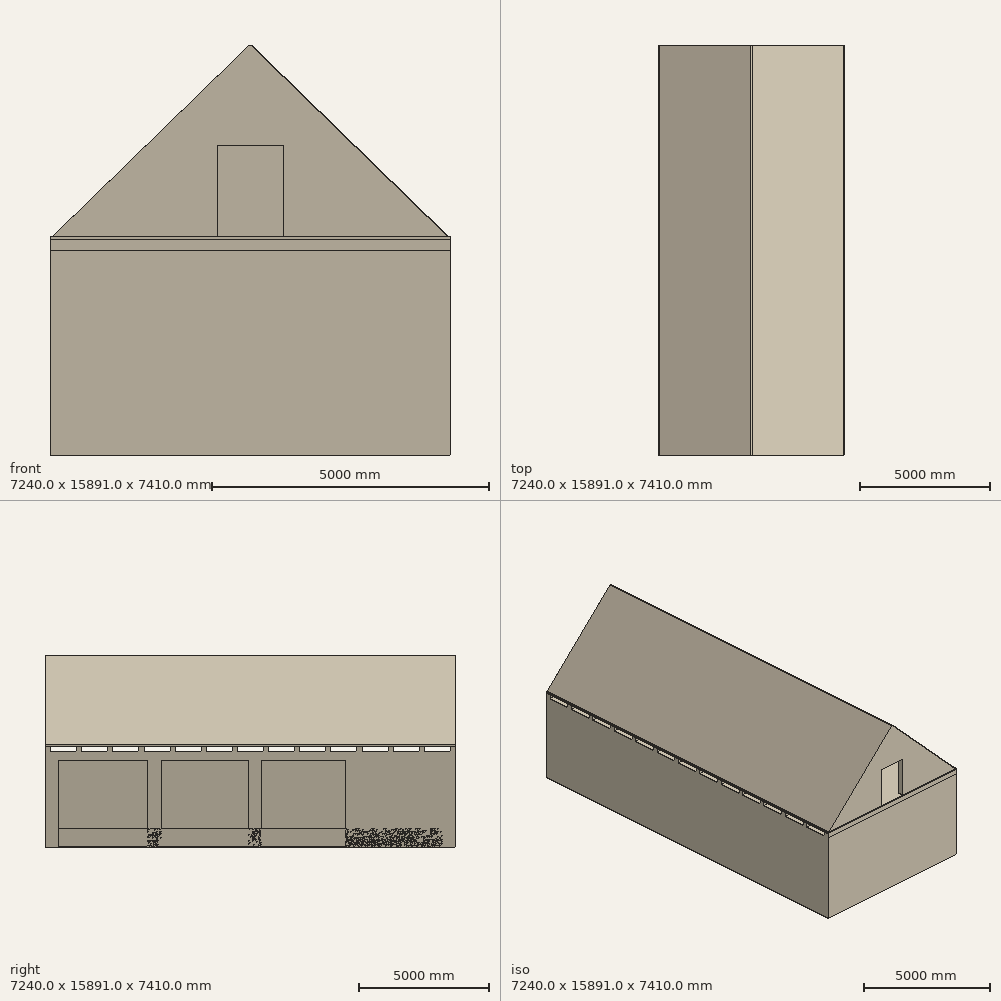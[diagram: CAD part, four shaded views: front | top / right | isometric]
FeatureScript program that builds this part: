
annotation { "Feature Type Name" : "Feature", "Feature Type Description" : "" }
export const myFeature = defineFeature(function(context is Context, id is Id, definition is map)
    precondition{}
    {
        {
            var Q0;
            Q0=qCreatedBy(makeId("Top.planeOp"),FACE);
            var sketch = newSketch(context, id + "F0", { "sketchPlane" : qUnion([Q0])});
            skLineSegment(sketch, "E0.bottom", {"start": v(-3374.35, 6436.17) * mm, "end": v(2825.65, 6436.17) * mm});
            skLineSegment(sketch, "E0.top", {"start": v(-3374.35, -8413.83) * mm, "end": v(2825.65, -8413.83) * mm});
            skLineSegment(sketch, "E0.left", {"start": v(-3374.35, 6436.17) * mm, "end": v(-3374.35, -8413.83) * mm});
            skLineSegment(sketch, "E0.right", {"start": v(2825.65, 6436.17) * mm, "end": v(2825.65, -8413.83) * mm});
            skLineSegment(sketch, "E1.0", {"start": v(-3894.35, 6956.17) * mm, "end": v(-3894.35, -8933.83) * mm});
            skLineSegment(sketch, "E1.1", {"start": v(-3894.35, 6956.17) * mm, "end": v(3345.65, 6956.17) * mm});
            skLineSegment(sketch, "E1.2", {"start": v(3345.65, 6956.17) * mm, "end": v(3345.65, -8933.83) * mm});
            skLineSegment(sketch, "E1.3", {"start": v(-3894.35, -8933.83) * mm, "end": v(3345.65, -8933.83) * mm});
            skLineSegment(sketch, "E2", {"start": v(2825.65, -8413.83) * mm, "end": v(3345.65, -8413.83) * mm});
            skLineSegment(sketch, "E3", {"start": v(2825.65, -4963.83) * mm, "end": v(3345.65, -4963.83) * mm});
            skLineSegment(sketch, "E4", {"start": v(2825.65, -4443.83) * mm, "end": v(3345.65, -4443.83) * mm});
            skLineSegment(sketch, "E5", {"start": v(2825.65, -1063.83) * mm, "end": v(3345.65, -1063.83) * mm});
            skLineSegment(sketch, "E6", {"start": v(2825.65, -543.83) * mm, "end": v(3345.65, -543.83) * mm});
            skLineSegment(sketch, "E7", {"start": v(2825.65, 2696.17) * mm, "end": v(3345.65, 2696.17) * mm});
            skSolve(sketch);
        }
        {
            var Q0;
            {var subQ5=sQuery(id+"F0.wireOp",EDGE,"E0.bottom");Q0=makeQuery(id+"F0.imprint","IMPRINT",FACE,{"disambiguationData":[TD([[makeQuery(id+"F0.imprint","IMPRINT",EDGE,{"derivedFrom":subQ5}),1.0]])]});}
            var Q1;
            {var subQ1=sQuery(id+"F0.wireOp",EDGE,"E0.bottom");Q1=makeQuery(id+"F0.imprint","IMPRINT",FACE,{"disambiguationData":[TD([[makeQuery(id+"F0.imprint","IMPRINT",EDGE,{"derivedFrom":subQ1}),-1.0]])]});}
            var Q2;
            {var subQ0=sQuery(id+"F0.wireOp",EDGE,"E6");Q2=makeQuery(id+"F0.imprint","IMPRINT",FACE,{"disambiguationData":[TD([[makeQuery(id+"F0.imprint","IMPRINT",EDGE,{"derivedFrom":subQ0}),1.0]])]});}
            var Q3;
            {var subQ0=sQuery(id+"F0.wireOp",EDGE,"E5");Q3=makeQuery(id+"F0.imprint","IMPRINT",FACE,{"disambiguationData":[TD([[makeQuery(id+"F0.imprint","IMPRINT",EDGE,{"derivedFrom":subQ0}),1.0]])]});}
            var Q4;
            {var subQ0=sQuery(id+"F0.wireOp",EDGE,"E4");Q4=makeQuery(id+"F0.imprint","IMPRINT",FACE,{"disambiguationData":[TD([[makeQuery(id+"F0.imprint","IMPRINT",EDGE,{"derivedFrom":subQ0}),1.0]])]});}
            var Q5;
            {var subQ0=sQuery(id+"F0.wireOp",EDGE,"E2");Q5=makeQuery(id+"F0.imprint","IMPRINT",FACE,{"disambiguationData":[TD([[makeQuery(id+"F0.imprint","IMPRINT",EDGE,{"derivedFrom":subQ0}),1.0]])]});}
            var Q6;
            {var subQ0=sQuery(id+"F0.wireOp",EDGE,"E3");Q6=makeQuery(id+"F0.imprint","IMPRINT",FACE,{"disambiguationData":[TD([[makeQuery(id+"F0.imprint","IMPRINT",EDGE,{"derivedFrom":subQ0}),1.0]])]});}
            extrude(context, id + "F1", {"entities" : qUnion([Q0, Q1, Q2, Q3, Q4, Q5, Q6]), "oppositeDirection" : true, "depth" : 10 * mm, "offsetDistance" : 25 * mm});
        }
        {
            var Q0;
            {var subQ0=sQuery(id+"F0.wireOp",EDGE,"E5");Q0=makeQuery(id+"F0.imprint","IMPRINT",FACE,{"disambiguationData":[TD([[makeQuery(id+"F0.imprint","IMPRINT",EDGE,{"derivedFrom":subQ0}),1.0]])]});}
            var Q1;
            {var subQ0=sQuery(id+"F0.wireOp",EDGE,"E3");Q1=makeQuery(id+"F0.imprint","IMPRINT",FACE,{"disambiguationData":[TD([[makeQuery(id+"F0.imprint","IMPRINT",EDGE,{"derivedFrom":subQ0}),1.0]])]});}
            var Q2;
            {var subQ5=sQuery(id+"F0.wireOp",EDGE,"E0.bottom");Q2=makeQuery(id+"F0.imprint","IMPRINT",FACE,{"disambiguationData":[TD([[makeQuery(id+"F0.imprint","IMPRINT",EDGE,{"derivedFrom":subQ5}),1.0]])]});}
            extrude(context, id + "F2", {"entities" : qUnion([Q0, Q1, Q2]), "operationType" : NewBodyOperationType.ADD, "depth" : 3350 * mm, "offsetDistance" : 25 * mm});
        }
        {
            var Q0;
            Q0=makeQuery(id+"F2.opExtrude","CAP_FACE",FACE,{"disambiguationData":[OSD([sQuery(id+"F0.wireOp",EDGE,"E0.bottom"),sQuery(id+"F0.wireOp",EDGE,"E0.top"),sQuery(id+"F0.wireOp",EDGE,"E0.left"),sQuery(id+"F0.wireOp",EDGE,"E0.right"),sQuery(id+"F0.wireOp",EDGE,"E1.0"),sQuery(id+"F0.wireOp",EDGE,"E1.1"),sQuery(id+"F0.wireOp",EDGE,"E1.2"),sQuery(id+"F0.wireOp",EDGE,"E1.3"),sQuery(id+"F0.wireOp",EDGE,"E2"),sQuery(id+"F0.wireOp",EDGE,"E7")])],"isStart":false});
            var sketch = newSketch(context, id + "F3", { "sketchPlane" : qUnion([Q0])});
            skLineSegment(sketch, "E8.bottom", {"start": v(-3894.35, 6956.17) * mm, "end": v(3345.65, 6956.17) * mm});
            skLineSegment(sketch, "E8.top", {"start": v(-3894.35, -8933.83) * mm, "end": v(3345.65, -8933.83) * mm});
            skLineSegment(sketch, "E8.left", {"start": v(-3894.35, 6956.17) * mm, "end": v(-3894.35, -8933.83) * mm});
            skLineSegment(sketch, "E8.right", {"start": v(3345.65, 6956.17) * mm, "end": v(3345.65, -8933.83) * mm});
            skLineSegment(sketch, "E9.bottom", {"start": v(2825.65, 6436.17) * mm, "end": v(-3374.35, 6436.17) * mm});
            skLineSegment(sketch, "E9.top", {"start": v(2825.65, -8413.83) * mm, "end": v(-3374.35, -8413.83) * mm});
            skLineSegment(sketch, "E9.left", {"start": v(2825.65, 6436.17) * mm, "end": v(2825.65, -8413.83) * mm});
            skLineSegment(sketch, "E9.right", {"start": v(-3374.35, 6436.17) * mm, "end": v(-3374.35, -8413.83) * mm});
            skSolve(sketch);
        }
        {
            var Q0;
            {var subQ8=sQuery(id+"F3.wireOp",EDGE,"E8.bottom");Q0=makeQuery(id+"F3.imprint","IMPRINT",FACE,{"disambiguationData":[TD([[makeQuery(id+"F3.imprint","IMPRINT",EDGE,{"derivedFrom":subQ8}),-1.0]])]});}
            var Q1;
            {var subQ3=makeQuery(id+"F2.opExtrude","CAP_EDGE",EDGE,{"disambiguationData":[OSD([sQuery(id+"F0.wireOp",EDGE,"E7")])],"isStart":false});Q1=makeQuery(id+"F3.imprint","IMPRINT",FACE,{"disambiguationData":[TD([[makeQuery(id+"F3.imprint","IMPRINT",EDGE,{"derivedFrom":subQ3}),-1.0]])]});}
            extrude(context, id + "F4", {"entities" : qUnion([Q0, Q1]), "operationType" : NewBodyOperationType.ADD, "depth" : 350 * mm, "offsetDistance" : 25 * mm});
        }
        {
            var Q0;
            Q0=makeQuery(id+"F4.opExtrude","CAP_FACE",FACE,{"disambiguationData":[OSD([sQuery(id+"F3.wireOp",EDGE,"E8.bottom"),sQuery(id+"F3.wireOp",EDGE,"E8.top"),sQuery(id+"F3.wireOp",EDGE,"E8.left"),sQuery(id+"F3.wireOp",EDGE,"E8.right"),sQuery(id+"F3.wireOp",EDGE,"E9.bottom"),sQuery(id+"F3.wireOp",EDGE,"E9.top"),sQuery(id+"F3.wireOp",EDGE,"E9.left"),sQuery(id+"F3.wireOp",EDGE,"E9.right")])],"isStart":false});
            var sketch = newSketch(context, id + "F5", { "sketchPlane" : qUnion([Q0])});
            skLineSegment(sketch, "E10.bottom", {"start": v(3345.65, 6956.17) * mm, "end": v(-3894.35, 6956.17) * mm});
            skLineSegment(sketch, "E10.top", {"start": v(3345.65, 6756.17) * mm, "end": v(-3894.35, 6756.17) * mm});
            skLineSegment(sketch, "E10.left", {"start": v(3345.65, 6956.17) * mm, "end": v(3345.65, 6756.17) * mm});
            skLineSegment(sketch, "E10.right", {"start": v(-3894.35, 6956.17) * mm, "end": v(-3894.35, 6756.17) * mm});
            skLineSegment(sketch, "E11.bottom", {"start": v(3345.65, 5749.17) * mm, "end": v(-3894.35, 5749.17) * mm});
            skLineSegment(sketch, "E11.top", {"start": v(3345.65, 5549.17) * mm, "end": v(-3894.35, 5549.17) * mm});
            skLineSegment(sketch, "E11.left", {"start": v(3345.65, 5749.17) * mm, "end": v(3345.65, 5549.17) * mm});
            skLineSegment(sketch, "E11.right", {"start": v(-3894.35, 5749.17) * mm, "end": v(-3894.35, 5549.17) * mm});
            skLineSegment(sketch, "E12.bottom", {"start": v(3345.65, 4542.17) * mm, "end": v(-3894.35, 4542.17) * mm});
            skLineSegment(sketch, "E12.top", {"start": v(3345.65, 4342.17) * mm, "end": v(-3894.35, 4342.17) * mm});
            skLineSegment(sketch, "E12.left", {"start": v(3345.65, 4542.17) * mm, "end": v(3345.65, 4342.17) * mm});
            skLineSegment(sketch, "E12.right", {"start": v(-3894.35, 4542.17) * mm, "end": v(-3894.35, 4342.17) * mm});
            skLineSegment(sketch, "E13.bottom", {"start": v(3345.65, 3335.17) * mm, "end": v(-3894.35, 3335.17) * mm});
            skLineSegment(sketch, "E13.top", {"start": v(3345.65, 3135.17) * mm, "end": v(-3894.35, 3135.17) * mm});
            skLineSegment(sketch, "E13.left", {"start": v(3345.65, 3335.17) * mm, "end": v(3345.65, 3135.17) * mm});
            skLineSegment(sketch, "E13.right", {"start": v(-3894.35, 3335.17) * mm, "end": v(-3894.35, 3135.17) * mm});
            skLineSegment(sketch, "E14.bottom", {"start": v(3345.65, 2128.17) * mm, "end": v(-3894.35, 2128.17) * mm});
            skLineSegment(sketch, "E14.top", {"start": v(3345.65, 1928.17) * mm, "end": v(-3894.35, 1928.17) * mm});
            skLineSegment(sketch, "E14.left", {"start": v(3345.65, 2128.17) * mm, "end": v(3345.65, 1928.17) * mm});
            skLineSegment(sketch, "E14.right", {"start": v(-3894.35, 2128.17) * mm, "end": v(-3894.35, 1928.17) * mm});
            skLineSegment(sketch, "E15.bottom", {"start": v(3345.65, 921.17) * mm, "end": v(-3894.35, 921.17) * mm});
            skLineSegment(sketch, "E15.top", {"start": v(3345.65, 721.17) * mm, "end": v(-3894.35, 721.17) * mm});
            skLineSegment(sketch, "E15.left", {"start": v(3345.65, 921.17) * mm, "end": v(3345.65, 721.17) * mm});
            skLineSegment(sketch, "E15.right", {"start": v(-3894.35, 921.17) * mm, "end": v(-3894.35, 721.17) * mm});
            skLineSegment(sketch, "E16.bottom", {"start": v(3345.65, -285.83) * mm, "end": v(-3894.35, -285.83) * mm});
            skLineSegment(sketch, "E16.top", {"start": v(3345.65, -485.83) * mm, "end": v(-3894.35, -485.83) * mm});
            skLineSegment(sketch, "E16.left", {"start": v(3345.65, -285.83) * mm, "end": v(3345.65, -485.83) * mm});
            skLineSegment(sketch, "E16.right", {"start": v(-3894.35, -285.83) * mm, "end": v(-3894.35, -485.83) * mm});
            skLineSegment(sketch, "E17.bottom", {"start": v(3345.65, -1492.83) * mm, "end": v(-3894.35, -1492.83) * mm});
            skLineSegment(sketch, "E17.top", {"start": v(3345.65, -1692.83) * mm, "end": v(-3894.35, -1692.83) * mm});
            skLineSegment(sketch, "E17.left", {"start": v(3345.65, -1492.83) * mm, "end": v(3345.65, -1692.83) * mm});
            skLineSegment(sketch, "E17.right", {"start": v(-3894.35, -1492.83) * mm, "end": v(-3894.35, -1692.83) * mm});
            skLineSegment(sketch, "E18.bottom", {"start": v(3345.65, -2699.83) * mm, "end": v(-3894.35, -2699.83) * mm});
            skLineSegment(sketch, "E18.top", {"start": v(3345.65, -2899.83) * mm, "end": v(-3894.35, -2899.83) * mm});
            skLineSegment(sketch, "E18.left", {"start": v(3345.65, -2699.83) * mm, "end": v(3345.65, -2899.83) * mm});
            skLineSegment(sketch, "E18.right", {"start": v(-3894.35, -2699.83) * mm, "end": v(-3894.35, -2899.83) * mm});
            skLineSegment(sketch, "E19.bottom", {"start": v(3345.65, -3906.83) * mm, "end": v(-3894.35, -3906.83) * mm});
            skLineSegment(sketch, "E19.top", {"start": v(3345.65, -4106.83) * mm, "end": v(-3894.35, -4106.83) * mm});
            skLineSegment(sketch, "E19.left", {"start": v(3345.65, -3906.83) * mm, "end": v(3345.65, -4106.83) * mm});
            skLineSegment(sketch, "E19.right", {"start": v(-3894.35, -3906.83) * mm, "end": v(-3894.35, -4106.83) * mm});
            skLineSegment(sketch, "E20.bottom", {"start": v(-3894.35, -5113.83) * mm, "end": v(3345.65, -5113.83) * mm});
            skLineSegment(sketch, "E20.top", {"start": v(-3894.35, -5313.83) * mm, "end": v(3345.65, -5313.83) * mm});
            skLineSegment(sketch, "E20.left", {"start": v(-3894.35, -5113.83) * mm, "end": v(-3894.35, -5313.83) * mm});
            skLineSegment(sketch, "E20.right", {"start": v(3345.65, -5113.83) * mm, "end": v(3345.65, -5313.83) * mm});
            skLineSegment(sketch, "E21.bottom", {"start": v(3345.65, -6320.83) * mm, "end": v(-3894.35, -6320.83) * mm});
            skLineSegment(sketch, "E21.top", {"start": v(3345.65, -6520.83) * mm, "end": v(-3894.35, -6520.83) * mm});
            skLineSegment(sketch, "E21.left", {"start": v(3345.65, -6320.83) * mm, "end": v(3345.65, -6520.83) * mm});
            skLineSegment(sketch, "E21.right", {"start": v(-3894.35, -6320.83) * mm, "end": v(-3894.35, -6520.83) * mm});
            skLineSegment(sketch, "E22", {"start": v(-274.35, 5549.17) * mm, "end": v(-274.35, 4542.17) * mm, "construction": true});
            skLineSegment(sketch, "E23", {"start": v(-274.35, 4342.17) * mm, "end": v(-274.35, 3335.17) * mm, "construction": true});
            skLineSegment(sketch, "E24", {"start": v(-274.35, 3135.17) * mm, "end": v(-274.35, 2128.17) * mm, "construction": true});
            skLineSegment(sketch, "E25", {"start": v(-274.35, 1928.17) * mm, "end": v(-274.35, 921.17) * mm, "construction": true});
            skLineSegment(sketch, "E26", {"start": v(-274.35, 721.17) * mm, "end": v(-274.35, -285.83) * mm, "construction": true});
            skLineSegment(sketch, "E27", {"start": v(-274.35, -485.83) * mm, "end": v(-274.35, -1492.83) * mm, "construction": true});
            skLineSegment(sketch, "E28", {"start": v(-274.35, -1692.83) * mm, "end": v(-274.35, -2699.83) * mm, "construction": true});
            skLineSegment(sketch, "E29", {"start": v(-274.35, 5749.17) * mm, "end": v(-274.35, 6756.17) * mm, "construction": true});
            skLineSegment(sketch, "E30", {"start": v(-274.35, -2899.83) * mm, "end": v(-274.35, -3906.83) * mm, "construction": true});
            skLineSegment(sketch, "E31", {"start": v(-274.35, -4106.83) * mm, "end": v(-274.35, -5113.83) * mm, "construction": true});
            skLineSegment(sketch, "E32", {"start": v(-274.35, -5313.83) * mm, "end": v(-274.35, -6320.83) * mm, "construction": true});
            skLineSegment(sketch, "E33.bottom", {"start": v(-3894.35, -7527.83) * mm, "end": v(3345.65, -7527.83) * mm});
            skLineSegment(sketch, "E33.top", {"start": v(-3894.35, -7727.83) * mm, "end": v(3345.65, -7727.83) * mm});
            skLineSegment(sketch, "E33.left", {"start": v(-3894.35, -7527.83) * mm, "end": v(-3894.35, -7727.83) * mm});
            skLineSegment(sketch, "E33.right", {"start": v(3345.65, -7527.83) * mm, "end": v(3345.65, -7727.83) * mm});
            skLineSegment(sketch, "E34.bottom", {"start": v(3345.65, -8734.83) * mm, "end": v(-3894.35, -8734.83) * mm});
            skLineSegment(sketch, "E34.top", {"start": v(3345.65, -8934.83) * mm, "end": v(-3894.35, -8934.83) * mm});
            skLineSegment(sketch, "E34.left", {"start": v(3345.65, -8734.83) * mm, "end": v(3345.65, -8934.83) * mm});
            skLineSegment(sketch, "E34.right", {"start": v(-3894.35, -8734.83) * mm, "end": v(-3894.35, -8934.83) * mm});
            skLineSegment(sketch, "E35", {"start": v(-274.35, -6520.83) * mm, "end": v(-274.35, -7527.83) * mm, "construction": true});
            skLineSegment(sketch, "E36", {"start": v(-274.35, -7727.83) * mm, "end": v(-274.35, -8734.83) * mm, "construction": true});
            skSolve(sketch);
        }
        {
            var Q0;
            Q0 = qSketchRegion(id + "F5", true);
            extrude(context, id + "F6", {"entities" : qUnion([Q0]), "operationType" : NewBodyOperationType.ADD, "depth" : 200 * mm, "offsetDistance" : 25 * mm});
        }
        {
            var Q0;
            Q0=makeQuery(id+"F6.opExtrude","CAP_FACE",FACE,{"disambiguationData":[OSD([sQuery(id+"F5.wireOp",EDGE,"E17.bottom"),sQuery(id+"F5.wireOp",EDGE,"E17.top"),sQuery(id+"F5.wireOp",EDGE,"E17.left"),sQuery(id+"F5.wireOp",EDGE,"E17.right")])],"isStart":false});
            var sketch = newSketch(context, id + "F7", { "sketchPlane" : qUnion([Q0])});
            skLineSegment(sketch, "E37.bottom", {"start": v(3345.65, 6956.17) * mm, "end": v(-3894.35, 6956.17) * mm});
            skLineSegment(sketch, "E37.top", {"start": v(3345.65, -8933.83) * mm, "end": v(-3894.35, -8933.83) * mm});
            skLineSegment(sketch, "E37.left", {"start": v(3345.65, 6956.17) * mm, "end": v(3345.65, -8933.83) * mm});
            skLineSegment(sketch, "E37.right", {"start": v(-3894.35, 6956.17) * mm, "end": v(-3894.35, -8933.83) * mm});
            skSolve(sketch);
        }
        {
            var Q0;
            Q0 = qSketchRegion(id + "F7", true);
            extrude(context, id + "F8", {"entities" : qUnion([Q0]), "depth" : 3500 * mm, "offsetDistance" : 25 * mm});
        }
        {
            var Q0;
            Q0=makeQuery(id+"F8.opExtrude","CAP_EDGE",EDGE,{"disambiguationData":[OSD([sQuery(id+"F7.wireOp",EDGE,"E37.right")])],"isStart":false});
            var Q1;
            Q1=makeQuery(id+"F8.opExtrude","CAP_EDGE",EDGE,{"disambiguationData":[OSD([sQuery(id+"F7.wireOp",EDGE,"E37.left")])],"isStart":false});
            chamfer(context, id + "F9", {"entities" : qUnion([Q0, Q1]), "chamferType" : ChamferType.TWO_OFFSETS, "width1" : 3600 * mm, "oppositeDirection" : false, "width2" : 3500 * mm, "tangentPropagation" : true});
        }
        {
            var Q0;
            Q0=makeQuery(id+"F8.opExtrude","CAP_FACE",FACE,{"disambiguationData":[OSD([sQuery(id+"F7.wireOp",EDGE,"E37.bottom"),sQuery(id+"F7.wireOp",EDGE,"E37.top"),sQuery(id+"F7.wireOp",EDGE,"E37.left"),sQuery(id+"F7.wireOp",EDGE,"E37.right")])],"isStart":true});
            shell(context, id + "F10", {"entities" : qUnion([Q0]), "thickness" : 260 * mm});
        }
        {
            var Q0;
            Q0=makeQuery(id+"F8.opExtrude","SWEPT_FACE",FACE,{"disambiguationData":[OSD([sQuery(id+"F7.wireOp",EDGE,"E37.top")])]});
            var sketch = newSketch(context, id + "F11", { "sketchPlane" : qUnion([Q0])});
            skLineSegment(sketch, "E38", {"start": v(-274.35, 3900) * mm, "end": v(-274.35, 5889.81) * mm, "construction": true});
            skLineSegment(sketch, "E39.bottom", {"start": v(325.65, 3900) * mm, "end": v(-874.35, 3900) * mm});
            skLineSegment(sketch, "E39.top", {"start": v(325.65, 5600) * mm, "end": v(-874.35, 5600) * mm});
            skLineSegment(sketch, "E39.left", {"start": v(325.65, 3900) * mm, "end": v(325.65, 5600) * mm});
            skLineSegment(sketch, "E39.right", {"start": v(-874.35, 3900) * mm, "end": v(-874.35, 5600) * mm});
            skSolve(sketch);
        }
        {
            var Q0;
            Q0=makeQuery(id+"F11.imprint","IMPRINT",FACE,{"disambiguationData":[TD([[makeQuery(id+"F11.imprint","IMPRINT",EDGE,{"derivedFrom":sQuery(id+"F11.wireOp",EDGE,"E39.bottom")}),-1.0]])]});
            extrude(context, id + "F12", {"entities" : qUnion([Q0]), "operationType" : NewBodyOperationType.REMOVE, "oppositeDirection" : true, "depth" : 260 * mm, "offsetDistance" : 25 * mm});
        }
        {
            var Q0;
            Q0=makeQuery(id+"F1.opExtrude","CAP_FACE",FACE,{"disambiguationData":[OSD([sQuery(id+"F0.wireOp",EDGE,"E1.0"),sQuery(id+"F0.wireOp",EDGE,"E1.1"),sQuery(id+"F0.wireOp",EDGE,"E1.2"),sQuery(id+"F0.wireOp",EDGE,"E1.3")])],"isStart":true});
            var sketch = newSketch(context, id + "F13", { "sketchPlane" : qUnion([Q0])});
            skLineSegment(sketch, "E40.bottom", {"start": v(3345.65, -8413.83) * mm, "end": v(-3374.35, -8413.83) * mm});
            skLineSegment(sketch, "E40.top", {"start": v(3345.65, 6436.17) * mm, "end": v(-3374.35, 6436.17) * mm});
            skLineSegment(sketch, "E40.left", {"start": v(3345.65, -8413.83) * mm, "end": v(3345.65, 6436.17) * mm});
            skLineSegment(sketch, "E40.right", {"start": v(-3374.35, -8413.83) * mm, "end": v(-3374.35, 6436.17) * mm});
            skSolve(sketch);
        }
        {
            var Q0;
            Q0 = qSketchRegion(id + "F13", true);
            extrude(context, id + "F14", {"entities" : qUnion([Q0]), "depth" : 700 * mm, "offsetDistance" : 25 * mm});
        }
        {
            var Q0;
            Q0=makeQuery(id+"F6.opExtrude","CAP_FACE",FACE,{"disambiguationData":[OSD([sQuery(id+"F5.wireOp",EDGE,"E10.bottom"),sQuery(id+"F5.wireOp",EDGE,"E10.top"),sQuery(id+"F5.wireOp",EDGE,"E10.left"),sQuery(id+"F5.wireOp",EDGE,"E10.right")])],"isStart":false});
            var sketch = newSketch(context, id + "F15", { "sketchPlane" : qUnion([Q0])});
            skLineSegment(sketch, "E41.bottom", {"start": v(-3894.35, -8934.83) * mm, "end": v(3345.65, -8934.83) * mm});
            skLineSegment(sketch, "E41.top", {"start": v(-3894.35, 6956.17) * mm, "end": v(3345.65, 6956.17) * mm});
            skLineSegment(sketch, "E41.left", {"start": v(-3894.35, -8934.83) * mm, "end": v(-3894.35, 6956.17) * mm});
            skLineSegment(sketch, "E41.right", {"start": v(3345.65, -8934.83) * mm, "end": v(3345.65, 6956.17) * mm});
            skSolve(sketch);
        }
        {
            var Q0;
            Q0 = qSketchRegion(id + "F15", true);
            extrude(context, id + "F16", {"entities" : qUnion([Q0]), "depth" : 50 * mm, "offsetDistance" : 25 * mm});
        }
    });
